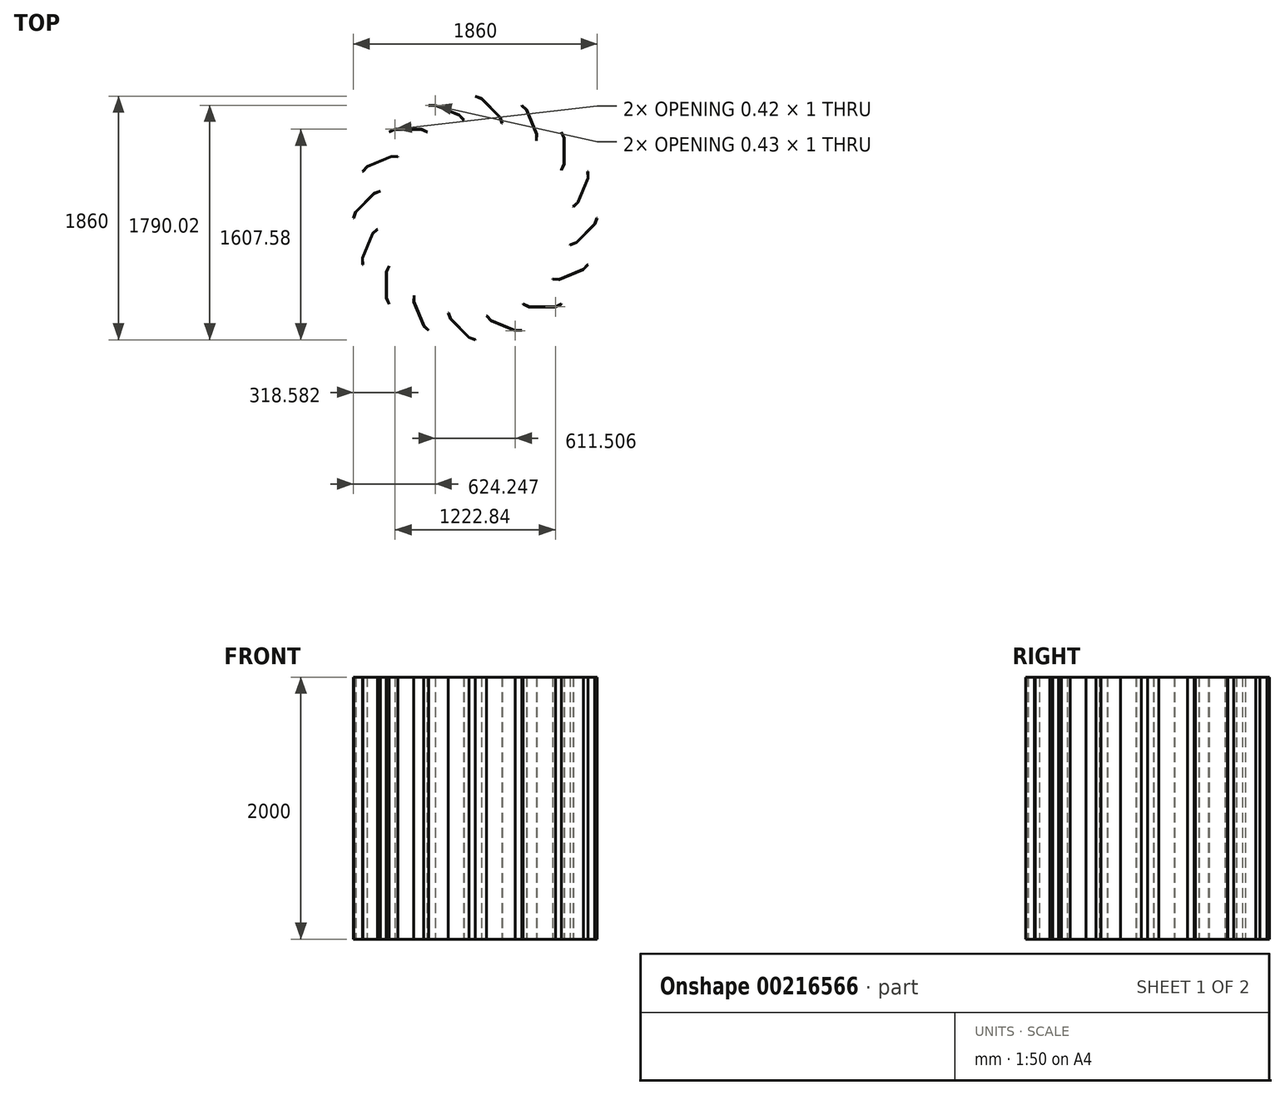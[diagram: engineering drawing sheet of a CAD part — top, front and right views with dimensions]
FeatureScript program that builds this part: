
annotation { "Feature Type Name" : "Feature", "Feature Type Description" : "" }
export const myFeature = defineFeature(function(context is Context, id is Id, definition is map)
    precondition{}
    {
        {
            var Q0;
            Q0=qCreatedBy(makeId("Top.planeOp"),FACE);
            var sketch = newSketch(context, id + "F0", { "sketchPlane" : qUnion([Q0])});
            skLineSegment(sketch, "E0", {"start": v(-935.22, -16.93) * mm, "end": v(-909.18, 54.61) * mm, "construction": true});
            skCircle(sketch, "E1", {"center": v(-929.06, 0) * mm, "radius": 1 * mm, "construction": true});
            skLineSegment(sketch, "E2", {"start": v(-913.13, 46.7) * mm, "end": v(-930, 0.34) * mm});
            skLineSegment(sketch, "E3", {"start": v(-930, 0.34) * mm, "end": v(-928.12, -0.34) * mm});
            skPoint(sketch, "E4", {"position": v(-930, 0.34) * mm});
            skCircle(sketch, "E5", {"center": v(0, 0) * mm, "radius": 930 * mm, "construction": true});
            skLineSegment(sketch, "E6", {"start": v(-921.76, 50.55) * mm, "end": v(-903.14, 43.78) * mm});
            skLineSegment(sketch, "E7", {"start": v(-911.25, 46.02) * mm, "end": v(-928.12, -0.34) * mm});
            skCircle(sketch, "E8", {"center": v(-911.96, 46.98) * mm, "radius": 1 * mm});
            skLineSegment(sketch, "E9", {"start": v(-920.18, 37.35) * mm, "end": v(-912.77, 44.76) * mm});
            skLineSegment(sketch, "E10", {"start": v(-911.96, 46.98) * mm, "end": v(-825.6, 133.35) * mm, "construction": true});
            skLineSegment(sketch, "E11", {"start": v(-912.2, 48.16) * mm, "end": v(-841.96, 118.4) * mm});
            skLineSegment(sketch, "E12", {"start": v(-911.96, 46.98) * mm, "end": v(-902.1, 37.12) * mm});
            skLineSegment(sketch, "E13", {"start": v(-864.34, 140.79) * mm, "end": v(-829.87, 106.32) * mm, "construction": true});
            skLineSegment(sketch, "E14.trimOffspring", {"start": v(-910.78, 46.75) * mm, "end": v(-840.54, 116.99) * mm});
            skArc(sketch, "E15.filletArc", {"start": v(-910.78, 46.75) * mm, "mid": v(-911.05, 46.4) * mm, "end": v(-911.25, 46.02) * mm});
            skPoint(sketch, "E16.visualSharp", {"position": v(-912.82, 47.53) * mm});
            skArc(sketch, "E16.filletArc", {"start": v(-912.2, 48.16) * mm, "mid": v(-912.74, 47.48) * mm, "end": v(-913.13, 46.7) * mm});
            skLineSegment(sketch, "E17.MirrorCS", {"start": v(-771.72, 188.64) * mm, "end": v(-841.96, 118.4) * mm});
            skLineSegment(sketch, "E18.MirrorCS", {"start": v(-770.3, 187.23) * mm, "end": v(-840.54, 116.99) * mm});
            skArc(sketch, "E19.MirrorCS", {"start": v(-771.72, 188.64) * mm, "mid": v(-771.04, 189.19) * mm, "end": v(-770.25, 189.57) * mm});
            skPoint(sketch, "E20.MirrorP", {"position": v(-771.09, 189.27) * mm});
            skArc(sketch, "E21.MirrorCS", {"start": v(-770.3, 187.23) * mm, "mid": v(-769.96, 187.5) * mm, "end": v(-769.57, 187.7) * mm});
            skLineSegment(sketch, "E22.MirrorCS", {"start": v(-770.25, 189.57) * mm, "end": v(-723.9, 206.45) * mm});
            skLineSegment(sketch, "E23.MirrorCS", {"start": v(-769.57, 187.7) * mm, "end": v(-723.21, 204.57) * mm});
            skLineSegment(sketch, "E24.MirrorCS", {"start": v(-723.9, 206.45) * mm, "end": v(-723.21, 204.57) * mm});
            skLineSegment(sketch, "E25", {"start": v(0, 0) * mm, "end": v(-956.54, 0) * mm, "construction": true});
            skSolve(sketch);
        }
        {
            var Q0;
            Q0 = qSketchRegion(id + "F0", true);
            extrude(context, id + "F1", {"entities" : qUnion([Q0]), "depth" : 2000 * mm});
        }
        {
            var Q0;
            Q0=qCreatedBy(makeId("Front.planeOp"),FACE);
            var sketch = newSketch(context, id + "F2", { "sketchPlane" : qUnion([Q0])});
            skLineSegment(sketch, "E26", {"start": v(0, -1523.6) * mm, "end": v(0, 2528.93) * mm, "construction": true});
            skSolve(sketch);
        }
        {
            var Q0;
            Q0=makeQuery(id+"F1.opExtrude","SWEPT_BODY",BODY,{"disambiguationData":[OSD([sQuery(id+"F0.wireOp",EDGE,"E2"),sQuery(id+"F0.wireOp",EDGE,"E3"),sQuery(id+"F0.wireOp",EDGE,"E6"),sQuery(id+"F0.wireOp",EDGE,"E7"),sQuery(id+"F0.wireOp",EDGE,"E8"),sQuery(id+"F0.wireOp",EDGE,"E11"),sQuery(id+"F0.wireOp",EDGE,"E12"),sQuery(id+"F0.wireOp",EDGE,"E14.trimOffspring"),sQuery(id+"F0.wireOp",EDGE,"E15.filletArc"),sQuery(id+"F0.wireOp",EDGE,"E16.filletArc"),sQuery(id+"F0.wireOp",EDGE,"E17.MirrorCS"),sQuery(id+"F0.wireOp",EDGE,"E18.MirrorCS"),sQuery(id+"F0.wireOp",EDGE,"E19.MirrorCS"),sQuery(id+"F0.wireOp",EDGE,"E21.MirrorCS"),sQuery(id+"F0.wireOp",EDGE,"E22.MirrorCS"),sQuery(id+"F0.wireOp",EDGE,"E23.MirrorCS"),sQuery(id+"F0.wireOp",EDGE,"E24.MirrorCS")])]});
            var Q1;
            Q1=sQuery(id+"F2.wireOp",EDGE,"E26");
            circularPattern(context, id + "F3", {"entities" : qUnion([Q0]), "axis" : qUnion([Q1]), "angle" : 360 * degree, "instanceCount" : 16, "equalSpace" : true});
        }
    });
